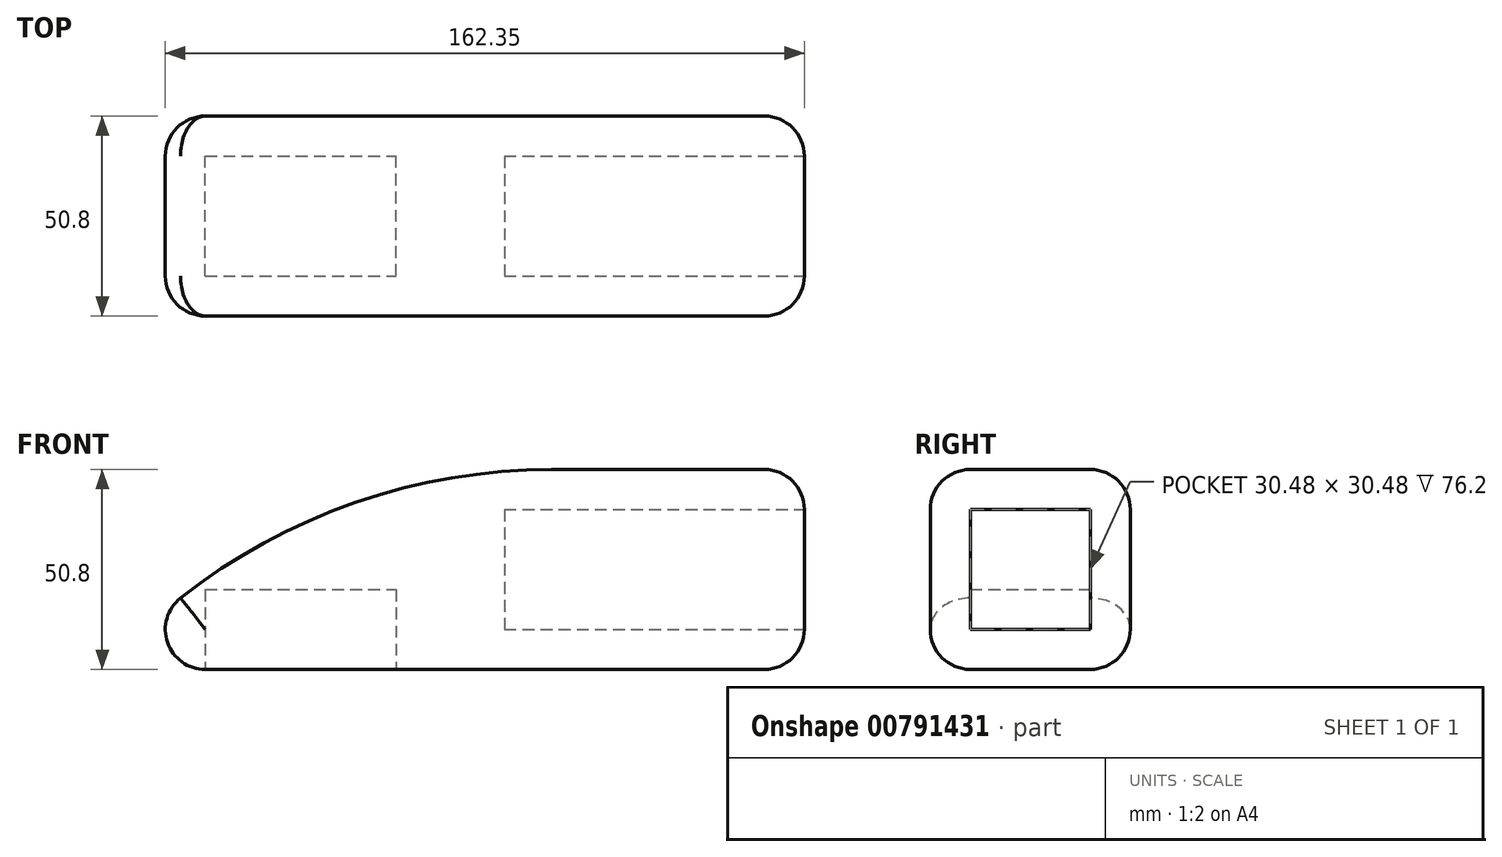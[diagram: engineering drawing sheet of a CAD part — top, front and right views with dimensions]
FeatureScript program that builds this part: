
annotation { "Feature Type Name" : "Feature", "Feature Type Description" : "" }
export const myFeature = defineFeature(function(context is Context, id is Id, definition is map)
    precondition{}
    {
        {
            var Q0;
            Q0=qCreatedBy(makeId("Top.planeOp"),FACE);
            var sketch = newSketch(context, id + "F0", { "sketchPlane" : qUnion([Q0])});
            skLineSegment(sketch, "E0.bottom", {"start": v(-85.9, 25.4) * mm, "end": v(91.9, 25.4) * mm});
            skLineSegment(sketch, "E0.top", {"start": v(-85.9, -25.4) * mm, "end": v(91.9, -25.4) * mm});
            skLineSegment(sketch, "E0.left", {"start": v(-85.9, 25.4) * mm, "end": v(-85.9, -25.4) * mm});
            skLineSegment(sketch, "E0.right", {"start": v(91.9, 25.4) * mm, "end": v(91.9, -25.4) * mm});
            skPoint(sketch, "E0.middle", {"position": v(3, 0) * mm});
            skSolve(sketch);
        }
        {
            var Q0;
            Q0=makeQuery(id+"F0.imprint","IMPRINT",FACE,{"disambiguationData":[TD([[makeQuery(id+"F0.imprint","IMPRINT",EDGE,{"derivedFrom":sQuery(id+"F0.wireOp",EDGE,"E0.bottom")}),-1.0]])]});
            extrude(context, id + "F1", {"entities" : qUnion([Q0]), "depth" : 50.8 * mm, "offsetDistance" : 25.4 * mm});
        }
        {
            var Q0;
            Q0=makeQuery(id+"F1.opExtrude","CAP_EDGE",EDGE,{"disambiguationData":[OSD([sQuery(id+"F0.wireOp",EDGE,"E0.left")])],"isStart":false});
            fillet(context, id + "F2", {"entities" : qUnion([Q0]), "radius" : 152.4 * mm, "tangentPropagation" : true, "allowEdgeOverflow" : false});
        }
        {
            var Q0;
            Q0=makeQuery(id+"F2.opFillet","BLEND_EDGE",EDGE,{"blendedFrom":[makeQuery(id+"F1.opExtrude","CAP_EDGE",EDGE,{"disambiguationData":[OSD([sQuery(id+"F0.wireOp",EDGE,"E0.left")])],"isStart":false}),makeQuery(id+"F1.opExtrude","SWEPT_FACE",FACE,{"disambiguationData":[OSD([sQuery(id+"F0.wireOp",EDGE,"E0.bottom")])]})],"blendedInto":[makeQuery(id+"F1.opExtrude","SWEPT_FACE",FACE,{"disambiguationData":[OSD([sQuery(id+"F0.wireOp",EDGE,"E0.bottom")])]})]});
            var Q1;
            Q1=makeQuery(id+"F2.opFillet","BLEND_EDGE",EDGE,{"blendedFrom":[makeQuery(id+"F1.opExtrude","CAP_EDGE",EDGE,{"disambiguationData":[OSD([sQuery(id+"F0.wireOp",EDGE,"E0.left")])],"isStart":false}),makeQuery(id+"F1.opExtrude","SWEPT_FACE",FACE,{"disambiguationData":[OSD([sQuery(id+"F0.wireOp",EDGE,"E0.top")])]})],"blendedInto":[makeQuery(id+"F1.opExtrude","SWEPT_FACE",FACE,{"disambiguationData":[OSD([sQuery(id+"F0.wireOp",EDGE,"E0.top")])]})]});
            fillet(context, id + "F3", {"entities" : qUnion([Q0, Q1]), "radius" : 10.16 * mm, "tangentPropagation" : true, "allowEdgeOverflow" : false});
        }
        {
            var Q0;
            {var subQ0=sQuery(id+"F0.wireOp",EDGE,"E0.left");Q0=makeQuery(id+"F2.opFillet","BLEND_EDGE",EDGE,{"blendedFrom":[makeQuery(id+"F1.opExtrude","CAP_EDGE",EDGE,{"disambiguationData":[OSD([subQ0])],"isStart":false}),makeQuery(id+"F1.opExtrude","CAP_FACE",FACE,{"disambiguationData":[OSD([sQuery(id+"F0.wireOp",EDGE,"E0.bottom"),sQuery(id+"F0.wireOp",EDGE,"E0.top"),subQ0,sQuery(id+"F0.wireOp",EDGE,"E0.right")])],"isStart":true})],"blendedInto":[makeQuery(id+"F1.opExtrude","CAP_FACE",FACE,{"disambiguationData":[OSD([sQuery(id+"F0.wireOp",EDGE,"E0.bottom"),sQuery(id+"F0.wireOp",EDGE,"E0.top"),subQ0,sQuery(id+"F0.wireOp",EDGE,"E0.right")])],"isStart":true})]});}
            var Q1;
            {var subQ0=sQuery(id+"F0.wireOp",EDGE,"E0.left");var subQ1=sQuery(id+"F0.wireOp",EDGE,"E0.top");Q1=makeQuery(id+"F3.opFillet","BLEND_EDGE",EDGE,{"blendedFrom":[makeQuery(id+"F2.opFillet","BLEND_EDGE",EDGE,{"blendedFrom":[makeQuery(id+"F1.opExtrude","CAP_EDGE",EDGE,{"disambiguationData":[OSD([subQ0])],"isStart":false}),makeQuery(id+"F1.opExtrude","SWEPT_FACE",FACE,{"disambiguationData":[OSD([subQ1])]})],"blendedInto":[makeQuery(id+"F1.opExtrude","SWEPT_FACE",FACE,{"disambiguationData":[OSD([subQ1])]})]}),makeQuery(id+"F1.opExtrude","CAP_FACE",FACE,{"disambiguationData":[OSD([sQuery(id+"F0.wireOp",EDGE,"E0.bottom"),subQ1,subQ0,sQuery(id+"F0.wireOp",EDGE,"E0.right")])],"isStart":true})],"blendedInto":[makeQuery(id+"F1.opExtrude","CAP_FACE",FACE,{"disambiguationData":[OSD([sQuery(id+"F0.wireOp",EDGE,"E0.bottom"),subQ1,subQ0,sQuery(id+"F0.wireOp",EDGE,"E0.right")])],"isStart":true})]});}
            var Q2;
            {var subQ0=sQuery(id+"F0.wireOp",EDGE,"E0.left");var subQ1=sQuery(id+"F0.wireOp",EDGE,"E0.bottom");Q2=makeQuery(id+"F3.opFillet","BLEND_EDGE",EDGE,{"blendedFrom":[makeQuery(id+"F2.opFillet","BLEND_EDGE",EDGE,{"blendedFrom":[makeQuery(id+"F1.opExtrude","CAP_EDGE",EDGE,{"disambiguationData":[OSD([subQ0])],"isStart":false}),makeQuery(id+"F1.opExtrude","SWEPT_FACE",FACE,{"disambiguationData":[OSD([subQ1])]})],"blendedInto":[makeQuery(id+"F1.opExtrude","SWEPT_FACE",FACE,{"disambiguationData":[OSD([subQ1])]})]}),makeQuery(id+"F1.opExtrude","CAP_FACE",FACE,{"disambiguationData":[OSD([subQ1,sQuery(id+"F0.wireOp",EDGE,"E0.top"),subQ0,sQuery(id+"F0.wireOp",EDGE,"E0.right")])],"isStart":true})],"blendedInto":[makeQuery(id+"F1.opExtrude","CAP_FACE",FACE,{"disambiguationData":[OSD([subQ1,sQuery(id+"F0.wireOp",EDGE,"E0.top"),subQ0,sQuery(id+"F0.wireOp",EDGE,"E0.right")])],"isStart":true})]});}
            fillet(context, id + "F4", {"entities" : qUnion([Q0, Q1, Q2]), "radius" : 10.16 * mm, "tangentPropagation" : true, "allowEdgeOverflow" : false});
        }
        {
            var Q0;
            Q0=makeQuery(id+"F1.opExtrude","CAP_EDGE",EDGE,{"disambiguationData":[OSD([sQuery(id+"F0.wireOp",EDGE,"E0.right")])],"isStart":false});
            fillet(context, id + "F5", {"entities" : qUnion([Q0]), "radius" : 10.16 * mm, "tangentPropagation" : true, "allowEdgeOverflow" : false});
        }
        {
            var Q0;
            Q0=makeQuery(id+"F1.opExtrude","SWEPT_FACE",FACE,{"disambiguationData":[OSD([sQuery(id+"F0.wireOp",EDGE,"E0.right")])]});
            extrude(context, id + "F6", {"entities" : qUnion([Q0]), "operationType" : NewBodyOperationType.REMOVE, "oppositeDirection" : true, "depth" : 76.2 * mm, "offsetDistance" : 25.4 * mm});
        }
        {
            var Q0;
            Q0=makeQuery(id+"F1.opExtrude","CAP_FACE",FACE,{"disambiguationData":[OSD([sQuery(id+"F0.wireOp",EDGE,"E0.bottom"),sQuery(id+"F0.wireOp",EDGE,"E0.top"),sQuery(id+"F0.wireOp",EDGE,"E0.left"),sQuery(id+"F0.wireOp",EDGE,"E0.right")])],"isStart":true});
            var sketch = newSketch(context, id + "F7", { "sketchPlane" : qUnion([Q0])});
            skLineSegment(sketch, "E1", {"start": v(-11.81, 15.24) * mm, "end": v(-11.81, -15.24) * mm});
            skSolve(sketch);
        }
        {
            var Q0;
            {var subQ0=sQuery(id+"F7.wireOp",EDGE,"E1");Q0=makeQuery(id+"F7.imprint","IMPRINT",FACE,{"disambiguationData":[TD([[makeQuery(id+"F7.imprint","IMPRINT",EDGE,{"derivedFrom":subQ0}),-1.0]])]});}
            extrude(context, id + "F8", {"entities" : qUnion([Q0]), "operationType" : NewBodyOperationType.REMOVE, "oppositeDirection" : true, "depth" : 20.32 * mm, "offsetDistance" : 25.4 * mm});
        }
    });
